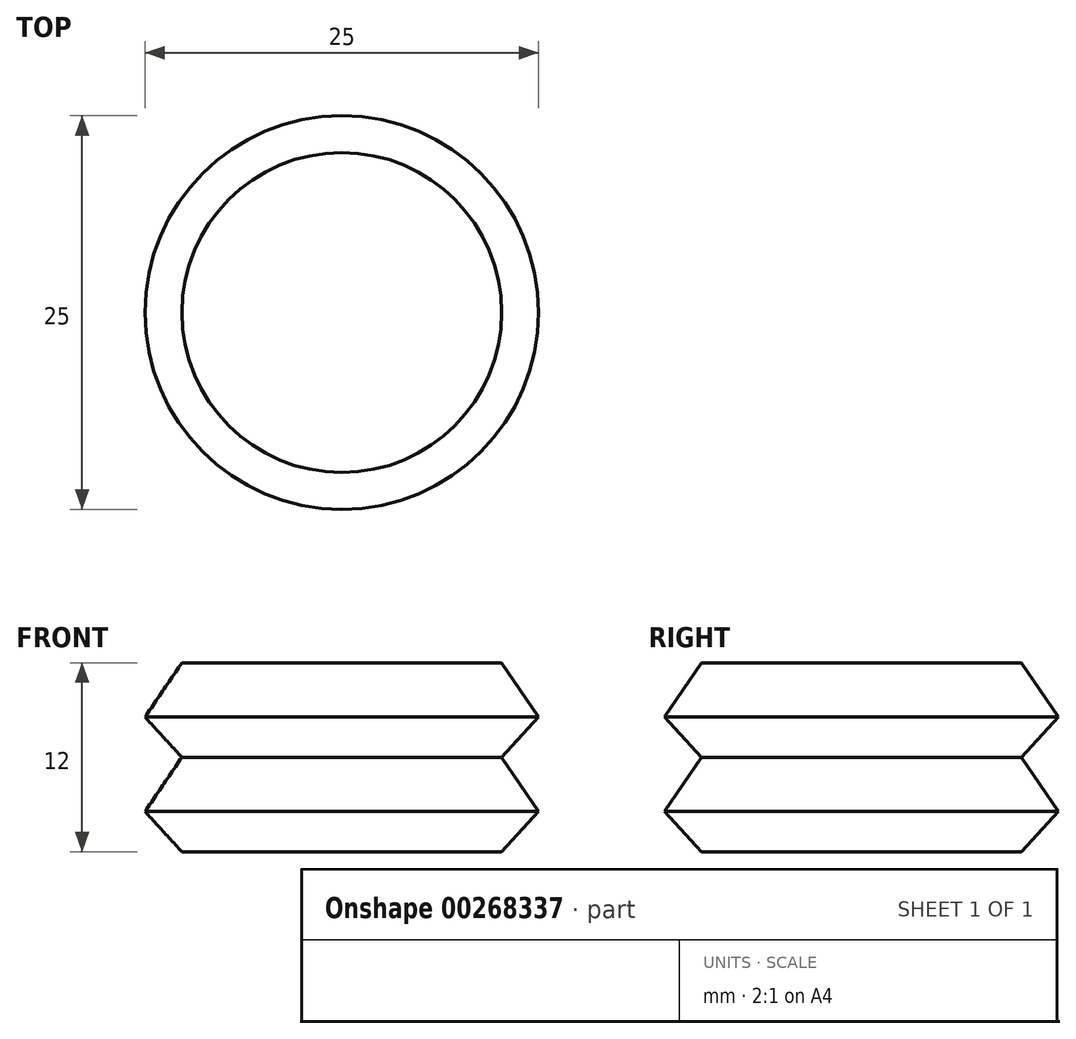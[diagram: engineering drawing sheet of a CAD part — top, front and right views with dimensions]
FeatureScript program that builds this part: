
annotation { "Feature Type Name" : "Feature", "Feature Type Description" : "" }
export const myFeature = defineFeature(function(context is Context, id is Id, definition is map)
    precondition{}
    {
        {
            var Q0;
            Q0=qCreatedBy(makeId("Front.planeOp"),FACE);
            var sketch = newSketch(context, id + "F0", { "sketchPlane" : qUnion([Q0])});
            skLineSegment(sketch, "E0", {"start": v(0, 32.82) * mm, "end": v(10.16, 32.82) * mm});
            skLineSegment(sketch, "E1", {"start": v(10.16, 32.82) * mm, "end": v(12.5, 29.37) * mm});
            skLineSegment(sketch, "E2", {"start": v(12.5, 29.37) * mm, "end": v(10.16, 26.82) * mm});
            skLineSegment(sketch, "E3", {"start": v(10.16, 26.82) * mm, "end": v(12.5, 23.37) * mm});
            skLineSegment(sketch, "E4", {"start": v(12.5, 23.37) * mm, "end": v(10.16, 20.82) * mm});
            skLineSegment(sketch, "E5", {"start": v(10.16, 20.82) * mm, "end": v(0, 20.82) * mm});
            skLineSegment(sketch, "E6", {"start": v(0, 20.82) * mm, "end": v(0, 32.82) * mm});
            skSolve(sketch);
        }
        {
            var Q0;
            Q0=qSketchRegion(id+"F0",true);
            var Q1;
            Q1=sQuery(id+"F0.wireOp",EDGE,"E6");
            revolve(context, id + "F1", {"entities" : qUnion([Q0]), "axis" : qUnion([Q1]), "revolveType" : RevolveType.FULL});
        }
    });
